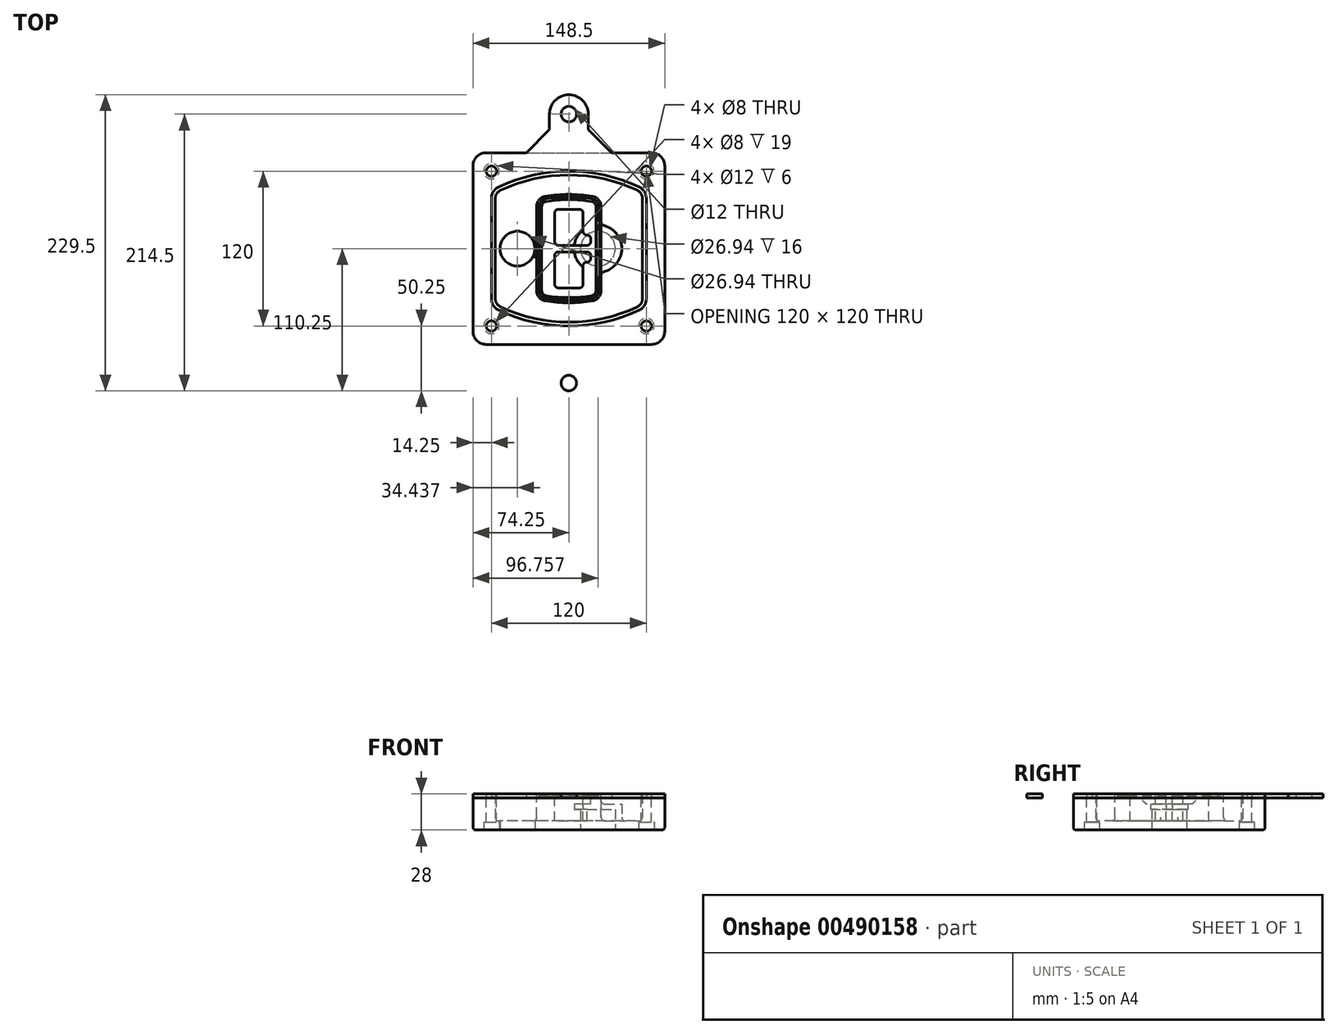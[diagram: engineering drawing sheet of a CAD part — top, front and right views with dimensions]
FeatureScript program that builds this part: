
annotation { "Feature Type Name" : "Feature", "Feature Type Description" : "" }
export const myFeature = defineFeature(function(context is Context, id is Id, definition is map)
    precondition{}
    {
        {
            var Q0;
            Q0=qCreatedBy(makeId("Top.planeOp"),FACE);
            var sketch = newSketch(context, id + "F0", { "sketchPlane" : qUnion([Q0])});
            skPoint(sketch, "E0.rect.middle", {"position": v(0, 0) * mm});
            skLineSegment(sketch, "E1.bottom", {"start": v(-64.25, -74.25) * mm, "end": v(64.25, -74.25) * mm});
            skLineSegment(sketch, "E1.top", {"start": v(-64.25, 74.25) * mm, "end": v(64.25, 74.25) * mm});
            skLineSegment(sketch, "E1.left", {"start": v(-74.25, -64.25) * mm, "end": v(-74.25, 64.25) * mm});
            skLineSegment(sketch, "E1.right", {"start": v(74.25, -64.25) * mm, "end": v(74.25, 64.25) * mm});
            skLineSegment(sketch, "E2", {"start": v(-74.25, 74.25) * mm, "end": v(74.25, -74.25) * mm, "construction": true});
            skLineSegment(sketch, "E3", {"start": v(74.25, 74.25) * mm, "end": v(-74.25, -74.25) * mm, "construction": true});
            skCircle(sketch, "E4", {"center": v(-60, 60) * mm, "radius": 4 * mm});
            skCircle(sketch, "E5", {"center": v(60, 60) * mm, "radius": 4 * mm});
            skCircle(sketch, "E6", {"center": v(60, -60) * mm, "radius": 4 * mm});
            skCircle(sketch, "E7", {"center": v(-60, -60) * mm, "radius": 4 * mm});
            skLineSegment(sketch, "E8", {"start": v(-60, 60) * mm, "end": v(60, 60) * mm, "construction": true});
            skLineSegment(sketch, "E9", {"start": v(60, 60) * mm, "end": v(60, -60) * mm, "construction": true});
            skLineSegment(sketch, "E10", {"start": v(60, -60) * mm, "end": v(-60, -60) * mm, "construction": true});
            skLineSegment(sketch, "E11", {"start": v(-60, -60) * mm, "end": v(-60, 60) * mm, "construction": true});
            skLineSegment(sketch, "E12", {"start": v(-60, 38.83) * mm, "end": v(-60, -38.83) * mm});
            skLineSegment(sketch, "E13", {"start": v(60, 38.83) * mm, "end": v(60, -38.83) * mm});
            skArc(sketch, "E14", {"start": v(54.26, 47.88) * mm, "mid": v(0, 60) * mm, "end": v(-54.26, 47.88) * mm});
            skArc(sketch, "E15", {"start": v(-54.26, -47.88) * mm, "mid": v(0, -60) * mm, "end": v(54.26, -47.88) * mm});
            skLineSegment(sketch, "E16", {"start": v(-60, 0) * mm, "end": v(60, 0) * mm, "construction": true});
            skPoint(sketch, "E17.visualSharp", {"position": v(-60, -45) * mm});
            skArc(sketch, "E17.filletArc", {"start": v(-60, -38.83) * mm, "mid": v(-58.44, -44.2) * mm, "end": v(-54.26, -47.88) * mm});
            skPoint(sketch, "E18.visualSharp", {"position": v(-60, 45) * mm});
            skArc(sketch, "E18.filletArc", {"start": v(-54.26, 47.88) * mm, "mid": v(-58.44, 44.2) * mm, "end": v(-60, 38.83) * mm});
            skPoint(sketch, "E19.visualSharp", {"position": v(60, 45) * mm});
            skArc(sketch, "E19.filletArc", {"start": v(60, 38.83) * mm, "mid": v(58.44, 44.2) * mm, "end": v(54.26, 47.88) * mm});
            skPoint(sketch, "E20.visualSharp", {"position": v(60, -45) * mm});
            skArc(sketch, "E20.filletArc", {"start": v(54.26, -47.88) * mm, "mid": v(58.44, -44.2) * mm, "end": v(60, -38.83) * mm});
            skPoint(sketch, "E21.visualSharp", {"position": v(-74.25, 74.25) * mm});
            skArc(sketch, "E21.filletArc", {"start": v(-64.25, 74.25) * mm, "mid": v(-71.32, 71.32) * mm, "end": v(-74.25, 64.25) * mm});
            skPoint(sketch, "E22.visualSharp", {"position": v(74.25, 74.25) * mm});
            skArc(sketch, "E22.filletArc", {"start": v(74.25, 64.25) * mm, "mid": v(71.32, 71.32) * mm, "end": v(64.25, 74.25) * mm});
            skPoint(sketch, "E23.visualSharp", {"position": v(74.25, -74.25) * mm});
            skArc(sketch, "E23.filletArc", {"start": v(64.25, -74.25) * mm, "mid": v(71.32, -71.32) * mm, "end": v(74.25, -64.25) * mm});
            skPoint(sketch, "E24.visualSharp", {"position": v(-74.25, -74.25) * mm});
            skArc(sketch, "E24.filletArc", {"start": v(-74.25, -64.25) * mm, "mid": v(-71.32, -71.32) * mm, "end": v(-64.25, -74.25) * mm});
            skArc(sketch, "E25.0", {"start": v(57, 38.83) * mm, "mid": v(55.9, 42.58) * mm, "end": v(52.98, 45.17) * mm});
            skLineSegment(sketch, "E25.1", {"start": v(57, 38.83) * mm, "end": v(57, -38.83) * mm});
            skArc(sketch, "E25.2", {"start": v(52.98, -45.17) * mm, "mid": v(55.9, -42.58) * mm, "end": v(57, -38.83) * mm});
            skArc(sketch, "E25.3", {"start": v(-52.98, -45.17) * mm, "mid": v(0, -57) * mm, "end": v(52.98, -45.17) * mm});
            skArc(sketch, "E25.4", {"start": v(-57, -38.83) * mm, "mid": v(-55.9, -42.58) * mm, "end": v(-52.98, -45.17) * mm});
            skArc(sketch, "E25.5", {"start": v(52.98, 45.17) * mm, "mid": v(0, 57) * mm, "end": v(-52.98, 45.17) * mm});
            skLineSegment(sketch, "E25.6", {"start": v(-57, 38.83) * mm, "end": v(-57, -38.83) * mm});
            skArc(sketch, "E25.7", {"start": v(-52.98, 45.17) * mm, "mid": v(-55.9, 42.58) * mm, "end": v(-57, 38.83) * mm});
            skArc(sketch, "E26.0", {"start": v(-55.96, 51.5) * mm, "mid": v(-61.82, 46.33) * mm, "end": v(-64, 38.83) * mm});
            skArc(sketch, "E26.1", {"start": v(55.96, 51.5) * mm, "mid": v(0, 64) * mm, "end": v(-55.96, 51.5) * mm});
            skArc(sketch, "E26.2", {"start": v(64, 38.83) * mm, "mid": v(61.82, 46.33) * mm, "end": v(55.96, 51.5) * mm});
            skLineSegment(sketch, "E26.3", {"start": v(64, 38.83) * mm, "end": v(64, -38.83) * mm});
            skArc(sketch, "E26.4", {"start": v(55.96, -51.5) * mm, "mid": v(61.82, -46.33) * mm, "end": v(64, -38.83) * mm});
            skLineSegment(sketch, "E26.5", {"start": v(-64, 38.83) * mm, "end": v(-64, -38.83) * mm});
            skArc(sketch, "E26.6", {"start": v(-55.96, -51.5) * mm, "mid": v(0, -64) * mm, "end": v(55.96, -51.5) * mm});
            skArc(sketch, "E26.7", {"start": v(-64, -38.83) * mm, "mid": v(-61.82, -46.33) * mm, "end": v(-55.96, -51.5) * mm});
            skSolve(sketch);
        }
        {
            var Q0;
            Q0=makeQuery(id+"F0.imprint","IMPRINT",FACE,{"disambiguationData":[TD([[makeQuery(id+"F0.imprint","IMPRINT",EDGE,{"derivedFrom":sQuery(id+"F0.wireOp",EDGE,"E1.bottom")}),1.0]])]});
            var Q1;
            Q1=makeQuery(id+"F0.imprint","IMPRINT",FACE,{"disambiguationData":[TD([[makeQuery(id+"F0.imprint","IMPRINT",EDGE,{"derivedFrom":sQuery(id+"F0.wireOp",EDGE,"E12")}),1.0]])]});
            var Q2;
            Q2=makeQuery(id+"F0.imprint","IMPRINT",FACE,{"disambiguationData":[TD([[makeQuery(id+"F0.imprint","IMPRINT",EDGE,{"derivedFrom":sQuery(id+"F0.wireOp",EDGE,"E25.0")}),1.0]])]});
            var Q3;
            Q3=makeQuery(id+"F0.imprint","IMPRINT",FACE,{"disambiguationData":[TD([[makeQuery(id+"F0.imprint","IMPRINT",EDGE,{"derivedFrom":sQuery(id+"F0.wireOp",EDGE,"E12")}),-1.0]])]});
            extrude(context, id + "F1", {"entities" : qUnion([Q0, Q1, Q2, Q3]), "oppositeDirection" : true, "depth" : 25 * mm});
        }
        {
            var Q0;
            Q0=makeQuery(id+"F0.imprint","IMPRINT",FACE,{"disambiguationData":[TD([[makeQuery(id+"F0.imprint","IMPRINT",EDGE,{"derivedFrom":sQuery(id+"F0.wireOp",EDGE,"E12")}),1.0]])]});
            extrude(context, id + "F2", {"entities" : qUnion([Q0]), "operationType" : NewBodyOperationType.ADD, "depth" : 3 * mm});
        }
        {
            var Q0;
            Q0=makeQuery(id+"F0.imprint","IMPRINT",FACE,{"disambiguationData":[TD([[makeQuery(id+"F0.imprint","IMPRINT",EDGE,{"derivedFrom":sQuery(id+"F0.wireOp",EDGE,"E25.0")}),1.0]])]});
            extrude(context, id + "F3", {"entities" : qUnion([Q0]), "operationType" : NewBodyOperationType.REMOVE, "oppositeDirection" : true, "depth" : 18 * mm});
        }
        {
            var Q0;
            Q0=makeQuery(id+"F2.opExtrude","CAP_FACE",FACE,{"disambiguationData":[OSD([sQuery(id+"F0.wireOp",EDGE,"E12"),sQuery(id+"F0.wireOp",EDGE,"E13"),sQuery(id+"F0.wireOp",EDGE,"E14"),sQuery(id+"F0.wireOp",EDGE,"E15"),sQuery(id+"F0.wireOp",EDGE,"E17.filletArc"),sQuery(id+"F0.wireOp",EDGE,"E18.filletArc"),sQuery(id+"F0.wireOp",EDGE,"E19.filletArc"),sQuery(id+"F0.wireOp",EDGE,"E20.filletArc"),sQuery(id+"F0.wireOp",EDGE,"E25.0"),sQuery(id+"F0.wireOp",EDGE,"E25.1"),sQuery(id+"F0.wireOp",EDGE,"E25.2"),sQuery(id+"F0.wireOp",EDGE,"E25.3"),sQuery(id+"F0.wireOp",EDGE,"E25.4"),sQuery(id+"F0.wireOp",EDGE,"E25.5"),sQuery(id+"F0.wireOp",EDGE,"E25.6"),sQuery(id+"F0.wireOp",EDGE,"E25.7")])],"isStart":false});
            var sketch = newSketch(context, id + "F4", { "sketchPlane" : qUnion([Q0])});
            skArc(sketch, "E27.0", {"start": v(-18.34, -40.45) * mm, "mid": v(0, -42) * mm, "end": v(18.34, -40.45) * mm});
            skArc(sketch, "E28.0", {"start": v(18.34, 40.45) * mm, "mid": v(0, 42) * mm, "end": v(-18.34, 40.45) * mm});
            skLineSegment(sketch, "E29", {"start": v(-25, 32.57) * mm, "end": v(-25, -32.57) * mm});
            skLineSegment(sketch, "E30", {"start": v(25, 32.57) * mm, "end": v(25, -32.57) * mm});
            skLineSegment(sketch, "E31", {"start": v(-25, 39.1) * mm, "end": v(25, 39.1) * mm, "construction": true});
            skLineSegment(sketch, "E32", {"start": v(-25, -39.1) * mm, "end": v(25, -39.1) * mm, "construction": true});
            skPoint(sketch, "E33.visualSharp", {"position": v(-25, 39.1) * mm});
            skArc(sketch, "E33.filletArc", {"start": v(-18.34, 40.45) * mm, "mid": v(-23.11, 37.73) * mm, "end": v(-25, 32.57) * mm});
            skPoint(sketch, "E34.visualSharp", {"position": v(25, 39.1) * mm});
            skArc(sketch, "E34.filletArc", {"start": v(25, 32.57) * mm, "mid": v(23.11, 37.73) * mm, "end": v(18.34, 40.45) * mm});
            skPoint(sketch, "E35.visualSharp", {"position": v(25, -39.1) * mm});
            skArc(sketch, "E35.filletArc", {"start": v(18.34, -40.45) * mm, "mid": v(23.11, -37.73) * mm, "end": v(25, -32.57) * mm});
            skPoint(sketch, "E36.visualSharp", {"position": v(-25, -39.1) * mm});
            skArc(sketch, "E36.filletArc", {"start": v(-25, -32.57) * mm, "mid": v(-23.11, -37.73) * mm, "end": v(-18.34, -40.45) * mm});
            skArc(sketch, "E37.0", {"start": v(52.98, 45.17) * mm, "mid": v(0, 57) * mm, "end": v(-52.98, 45.17) * mm});
            skArc(sketch, "E37.1", {"start": v(-52.98, 45.17) * mm, "mid": v(-55.9, 42.58) * mm, "end": v(-57, 38.83) * mm});
            skLineSegment(sketch, "E37.2", {"start": v(-57, 38.83) * mm, "end": v(-57, -38.83) * mm});
            skArc(sketch, "E37.3", {"start": v(-57, -38.83) * mm, "mid": v(-55.9, -42.58) * mm, "end": v(-52.98, -45.17) * mm});
            skArc(sketch, "E37.4", {"start": v(-52.98, -45.17) * mm, "mid": v(0, -57) * mm, "end": v(52.98, -45.17) * mm});
            skArc(sketch, "E37.5", {"start": v(52.98, -45.17) * mm, "mid": v(55.9, -42.58) * mm, "end": v(57, -38.83) * mm});
            skLineSegment(sketch, "E37.6", {"start": v(57, 38.83) * mm, "end": v(57, -38.83) * mm});
            skArc(sketch, "E37.7", {"start": v(57, 38.83) * mm, "mid": v(55.9, 42.58) * mm, "end": v(52.98, 45.17) * mm});
            skLineSegment(sketch, "E38.0", {"start": v(23, 32.57) * mm, "end": v(23, -32.57) * mm});
            skArc(sketch, "E38.1", {"start": v(18, -38.48) * mm, "mid": v(21.58, -36.44) * mm, "end": v(23, -32.57) * mm});
            skArc(sketch, "E38.2", {"start": v(-18, -38.48) * mm, "mid": v(0, -40) * mm, "end": v(18, -38.48) * mm});
            skArc(sketch, "E38.3", {"start": v(-23, -32.57) * mm, "mid": v(-21.58, -36.44) * mm, "end": v(-18, -38.48) * mm});
            skLineSegment(sketch, "E38.4", {"start": v(-23, 32.57) * mm, "end": v(-23, -32.57) * mm});
            skArc(sketch, "E38.5", {"start": v(23, 32.57) * mm, "mid": v(21.58, 36.44) * mm, "end": v(18, 38.48) * mm});
            skArc(sketch, "E38.6", {"start": v(-18, 38.48) * mm, "mid": v(-21.58, 36.44) * mm, "end": v(-23, 32.57) * mm});
            skArc(sketch, "E38.7", {"start": v(18, 38.48) * mm, "mid": v(0, 40) * mm, "end": v(-18, 38.48) * mm});
            skArc(sketch, "E39.0", {"start": v(21, 32.57) * mm, "mid": v(20.06, 35.15) * mm, "end": v(17.67, 36.5) * mm});
            skLineSegment(sketch, "E39.1", {"start": v(21, 32.57) * mm, "end": v(21, -32.57) * mm});
            skArc(sketch, "E39.2", {"start": v(17.67, -36.5) * mm, "mid": v(20.06, -35.15) * mm, "end": v(21, -32.57) * mm});
            skArc(sketch, "E39.3", {"start": v(-17.67, -36.5) * mm, "mid": v(0, -38) * mm, "end": v(17.67, -36.5) * mm});
            skArc(sketch, "E39.4", {"start": v(-21, -32.57) * mm, "mid": v(-20.06, -35.15) * mm, "end": v(-17.67, -36.5) * mm});
            skArc(sketch, "E39.5", {"start": v(17.67, 36.5) * mm, "mid": v(0, 38) * mm, "end": v(-17.67, 36.5) * mm});
            skLineSegment(sketch, "E39.6", {"start": v(-21, 32.57) * mm, "end": v(-21, -32.57) * mm});
            skArc(sketch, "E39.7", {"start": v(-17.67, 36.5) * mm, "mid": v(-20.06, 35.15) * mm, "end": v(-21, 32.57) * mm});
            skLineSegment(sketch, "E40", {"start": v(-25, 0) * mm, "end": v(25, 0) * mm, "construction": true});
            skLineSegment(sketch, "E41", {"start": v(-11, 5.5) * mm, "end": v(-11, 27.5) * mm});
            skLineSegment(sketch, "E42", {"start": v(-8, 30.5) * mm, "end": v(8, 30.5) * mm});
            skLineSegment(sketch, "E43", {"start": v(11, 27.5) * mm, "end": v(11, 13.5) * mm});
            skLineSegment(sketch, "E44", {"start": v(14, 10.5) * mm, "end": v(14, 10.5) * mm});
            skLineSegment(sketch, "E45", {"start": v(17, 7.5) * mm, "end": v(17, 5.5) * mm});
            skLineSegment(sketch, "E46", {"start": v(14, 2.5) * mm, "end": v(-8, 2.5) * mm});
            skPoint(sketch, "E47.visualSharp", {"position": v(-11, 30.5) * mm});
            skArc(sketch, "E47.filletArc", {"start": v(-8, 30.5) * mm, "mid": v(-10.12, 29.62) * mm, "end": v(-11, 27.5) * mm});
            skPoint(sketch, "E48.visualSharp", {"position": v(11, 30.5) * mm});
            skArc(sketch, "E48.filletArc", {"start": v(11, 27.5) * mm, "mid": v(10.12, 29.62) * mm, "end": v(8, 30.5) * mm});
            skPoint(sketch, "E49.visualSharp", {"position": v(11, 10.5) * mm});
            skArc(sketch, "E49.filletArc", {"start": v(11, 13.5) * mm, "mid": v(11.88, 11.38) * mm, "end": v(14, 10.5) * mm});
            skPoint(sketch, "E50.visualSharp", {"position": v(17, 10.5) * mm});
            skArc(sketch, "E50.filletArc", {"start": v(17, 7.5) * mm, "mid": v(16.12, 9.62) * mm, "end": v(14, 10.5) * mm});
            skPoint(sketch, "E51.visualSharp", {"position": v(17, 2.5) * mm});
            skArc(sketch, "E51.filletArc", {"start": v(14, 2.5) * mm, "mid": v(16.12, 3.38) * mm, "end": v(17, 5.5) * mm});
            skPoint(sketch, "E52.visualSharp", {"position": v(-11, 2.5) * mm});
            skArc(sketch, "E52.filletArc", {"start": v(-11, 5.5) * mm, "mid": v(-10.12, 3.38) * mm, "end": v(-8, 2.5) * mm});
            skLineSegment(sketch, "E53.0.MirrorCS", {"start": v(14, -2.5) * mm, "end": v(-8, -2.5) * mm});
            skArc(sketch, "E54.0.MirrorCS", {"start": v(-11, -5.5) * mm, "mid": v(-10.12, -3.38) * mm, "end": v(-8, -2.5) * mm});
            skLineSegment(sketch, "E55.0.MirrorCS", {"start": v(-11, -5.5) * mm, "end": v(-11, -27.5) * mm});
            skArc(sketch, "E56.0.MirrorCS", {"start": v(-8, -30.5) * mm, "mid": v(-10.12, -29.62) * mm, "end": v(-11, -27.5) * mm});
            skLineSegment(sketch, "E57.0.MirrorCS", {"start": v(-8, -30.5) * mm, "end": v(8, -30.5) * mm});
            skArc(sketch, "E58.0.MirrorCS", {"start": v(11, -27.5) * mm, "mid": v(10.12, -29.62) * mm, "end": v(8, -30.5) * mm});
            skLineSegment(sketch, "E59.0.MirrorCS", {"start": v(11, -27.5) * mm, "end": v(11, -13.5) * mm});
            skArc(sketch, "E60.0.MirrorCS", {"start": v(11, -13.5) * mm, "mid": v(11.88, -11.38) * mm, "end": v(14, -10.5) * mm});
            skArc(sketch, "E61.0.MirrorCS", {"start": v(17, -7.5) * mm, "mid": v(16.12, -9.62) * mm, "end": v(14, -10.5) * mm});
            skLineSegment(sketch, "E62.0.MirrorCS", {"start": v(17, -7.5) * mm, "end": v(17, -5.5) * mm});
            skArc(sketch, "E63.0.MirrorCS", {"start": v(14, -2.5) * mm, "mid": v(16.12, -3.38) * mm, "end": v(17, -5.5) * mm});
            skSolve(sketch);
        }
        {
            var Q0;
            Q0=makeQuery(id+"F4.imprint","IMPRINT",FACE,{"disambiguationData":[TD([[makeQuery(id+"F4.imprint","IMPRINT",EDGE,{"derivedFrom":sQuery(id+"F4.wireOp",EDGE,"E27.0")}),1.0]])]});
            var Q1;
            Q1=makeQuery(id+"F4.imprint","IMPRINT",FACE,{"disambiguationData":[TD([[makeQuery(id+"F4.imprint","IMPRINT",EDGE,{"derivedFrom":sQuery(id+"F4.wireOp",EDGE,"E38.0")}),-1.0]])]});
            var Q2;
            Q2=makeQuery(id+"F4.imprint","IMPRINT",FACE,{"disambiguationData":[TD([[makeQuery(id+"F4.imprint","IMPRINT",EDGE,{"derivedFrom":sQuery(id+"F4.wireOp",EDGE,"E39.0")}),1.0]])]});
            extrude(context, id + "F5", {"entities" : qUnion([Q0, Q1, Q2]), "operationType" : NewBodyOperationType.ADD, "endBound" : BoundingType.UP_TO_NEXT, "oppositeDirection" : true, "depth" : 25 * mm});
        }
        {
            var Q0;
            Q0=makeQuery(id+"F4.imprint","IMPRINT",FACE,{"disambiguationData":[TD([[makeQuery(id+"F4.imprint","IMPRINT",EDGE,{"derivedFrom":sQuery(id+"F4.wireOp",EDGE,"E38.0")}),-1.0]])]});
            extrude(context, id + "F6", {"entities" : qUnion([Q0]), "operationType" : NewBodyOperationType.REMOVE, "oppositeDirection" : true, "depth" : 2 * mm});
        }
        {
            var Q0;
            Q0=makeQuery(id+"F1.opExtrude","CAP_FACE",FACE,{"disambiguationData":[OSD([sQuery(id+"F0.wireOp",EDGE,"E1.bottom"),sQuery(id+"F0.wireOp",EDGE,"E1.top"),sQuery(id+"F0.wireOp",EDGE,"E1.left"),sQuery(id+"F0.wireOp",EDGE,"E1.right"),sQuery(id+"F0.wireOp",EDGE,"E4"),sQuery(id+"F0.wireOp",EDGE,"E5"),sQuery(id+"F0.wireOp",EDGE,"E6"),sQuery(id+"F0.wireOp",EDGE,"E7"),sQuery(id+"F0.wireOp",EDGE,"E21.filletArc"),sQuery(id+"F0.wireOp",EDGE,"E22.filletArc"),sQuery(id+"F0.wireOp",EDGE,"E23.filletArc"),sQuery(id+"F0.wireOp",EDGE,"E24.filletArc")])],"isStart":false});
            var sketch = newSketch(context, id + "F7", { "sketchPlane" : qUnion([Q0])});
            skCircle(sketch, "E64", {"center": v(22.5, 0) * mm, "radius": 13.47 * mm});
            skCircle(sketch, "E65", {"center": v(-39.81, 0) * mm, "radius": 13.47 * mm});
            skLineSegment(sketch, "E66", {"start": v(74.25, 0) * mm, "end": v(-74.25, 0) * mm});
            skCircle(sketch, "E67", {"center": v(22.5, 0) * mm, "radius": 18.47 * mm});
            skCircle(sketch, "E68", {"center": v(60, -60) * mm, "radius": 6 * mm});
            skCircle(sketch, "E69", {"center": v(-60, -60) * mm, "radius": 6 * mm});
            skCircle(sketch, "E70", {"center": v(-60, 60) * mm, "radius": 6 * mm});
            skCircle(sketch, "E71", {"center": v(60, 60) * mm, "radius": 6 * mm});
            skSolve(sketch);
        }
        {
            var Q0;
            {var subQ1=sQuery(id+"F7.wireOp",EDGE,"E66");var subQ4=sQuery(id+"F7.wireOp",EDGE,"E64");var subQ6=makeQuery(id+"F7.imprint","INTERSECT",VERTEX,{"disambiguationData":[OD(0.0)],"derivedFrom":[subQ4,subQ1]});Q0=makeQuery(id+"F7.imprint","IMPRINT",FACE,{"disambiguationData":[TD([[makeQuery(id+"F7.imprint","IMPRINT",EDGE,{"disambiguationData":[TD([[subQ6,-1.0]])],"derivedFrom":subQ4}),-1.0]])]});}
            var Q1;
            {var subQ0=sQuery(id+"F7.wireOp",EDGE,"E66");var subQ1=sQuery(id+"F7.wireOp",EDGE,"E64");var subQ3=makeQuery(id+"F7.imprint","INTERSECT",VERTEX,{"disambiguationData":[OD(0.0)],"derivedFrom":[subQ1,subQ0]});Q1=makeQuery(id+"F7.imprint","IMPRINT",FACE,{"disambiguationData":[TD([[makeQuery(id+"F7.imprint","IMPRINT",EDGE,{"disambiguationData":[TD([[subQ3,-1.0]])],"derivedFrom":subQ1}),1.0]])]});}
            var Q2;
            {var subQ0=sQuery(id+"F7.wireOp",EDGE,"E66");var subQ1=sQuery(id+"F7.wireOp",EDGE,"E64");var subQ3=makeQuery(id+"F7.imprint","INTERSECT",VERTEX,{"disambiguationData":[OD(0.0)],"derivedFrom":[subQ1,subQ0]});Q2=makeQuery(id+"F7.imprint","IMPRINT",FACE,{"disambiguationData":[TD([[makeQuery(id+"F7.imprint","IMPRINT",EDGE,{"disambiguationData":[TD([[subQ3,1.0]])],"derivedFrom":subQ1}),1.0]])]});}
            var Q3;
            {var subQ1=sQuery(id+"F7.wireOp",EDGE,"E66");var subQ4=sQuery(id+"F7.wireOp",EDGE,"E64");var subQ6=makeQuery(id+"F7.imprint","INTERSECT",VERTEX,{"disambiguationData":[OD(0.0)],"derivedFrom":[subQ4,subQ1]});Q3=makeQuery(id+"F7.imprint","IMPRINT",FACE,{"disambiguationData":[TD([[makeQuery(id+"F7.imprint","IMPRINT",EDGE,{"disambiguationData":[TD([[subQ6,1.0]])],"derivedFrom":subQ4}),-1.0]])]});}
            extrude(context, id + "F8", {"entities" : qUnion([Q0, Q1, Q2, Q3]), "operationType" : NewBodyOperationType.ADD, "oppositeDirection" : true, "depth" : 20 * mm});
        }
        {
            var Q0;
            {var subQ0=sQuery(id+"F7.wireOp",EDGE,"E66");var subQ1=sQuery(id+"F7.wireOp",EDGE,"E64");var subQ3=makeQuery(id+"F7.imprint","INTERSECT",VERTEX,{"disambiguationData":[OD(0.0)],"derivedFrom":[subQ1,subQ0]});Q0=makeQuery(id+"F7.imprint","IMPRINT",FACE,{"disambiguationData":[TD([[makeQuery(id+"F7.imprint","IMPRINT",EDGE,{"disambiguationData":[TD([[subQ3,-1.0]])],"derivedFrom":subQ1}),1.0]])]});}
            var Q1;
            {var subQ0=sQuery(id+"F7.wireOp",EDGE,"E66");var subQ1=sQuery(id+"F7.wireOp",EDGE,"E64");var subQ3=makeQuery(id+"F7.imprint","INTERSECT",VERTEX,{"disambiguationData":[OD(0.0)],"derivedFrom":[subQ1,subQ0]});Q1=makeQuery(id+"F7.imprint","IMPRINT",FACE,{"disambiguationData":[TD([[makeQuery(id+"F7.imprint","IMPRINT",EDGE,{"disambiguationData":[TD([[subQ3,1.0]])],"derivedFrom":subQ1}),1.0]])]});}
            extrude(context, id + "F9", {"entities" : qUnion([Q0, Q1]), "operationType" : NewBodyOperationType.REMOVE, "oppositeDirection" : true, "depth" : 16 * mm});
        }
        {
            var Q0;
            {var subQ0=sQuery(id+"F7.wireOp",EDGE,"E66");var subQ1=sQuery(id+"F7.wireOp",EDGE,"E65");var subQ3=makeQuery(id+"F7.imprint","INTERSECT",VERTEX,{"disambiguationData":[OD(0.0)],"derivedFrom":[subQ1,subQ0]});Q0=makeQuery(id+"F7.imprint","IMPRINT",FACE,{"disambiguationData":[TD([[makeQuery(id+"F7.imprint","IMPRINT",EDGE,{"disambiguationData":[TD([[subQ3,-1.0]])],"derivedFrom":subQ1}),1.0]])]});}
            var Q1;
            {var subQ0=sQuery(id+"F7.wireOp",EDGE,"E66");var subQ1=sQuery(id+"F7.wireOp",EDGE,"E65");var subQ3=makeQuery(id+"F7.imprint","INTERSECT",VERTEX,{"disambiguationData":[OD(0.0)],"derivedFrom":[subQ1,subQ0]});Q1=makeQuery(id+"F7.imprint","IMPRINT",FACE,{"disambiguationData":[TD([[makeQuery(id+"F7.imprint","IMPRINT",EDGE,{"disambiguationData":[TD([[subQ3,1.0]])],"derivedFrom":subQ1}),1.0]])]});}
            extrude(context, id + "F10", {"entities" : qUnion([Q0, Q1]), "operationType" : NewBodyOperationType.REMOVE, "oppositeDirection" : true, "depth" : 25 * mm});
        }
        {
            var Q0;
            Q0=makeQuery(id+"F7.imprint","IMPRINT",FACE,{"disambiguationData":[TD([[makeQuery(id+"F7.imprint","IMPRINT",EDGE,{"derivedFrom":sQuery(id+"F7.wireOp",EDGE,"E68")}),1.0]])]});
            var Q1;
            Q1=makeQuery(id+"F7.imprint","IMPRINT",FACE,{"disambiguationData":[TD([[makeQuery(id+"F7.imprint","IMPRINT",EDGE,{"derivedFrom":makeQuery(id+"F1.opExtrude","CAP_EDGE",EDGE,{"disambiguationData":[OSD([sQuery(id+"F0.wireOp",EDGE,"E5")])],"isStart":false})}),-1.0]])]});
            var Q2;
            Q2=makeQuery(id+"F7.imprint","IMPRINT",FACE,{"disambiguationData":[TD([[makeQuery(id+"F7.imprint","IMPRINT",EDGE,{"derivedFrom":sQuery(id+"F7.wireOp",EDGE,"E69")}),1.0]])]});
            var Q3;
            Q3=makeQuery(id+"F7.imprint","IMPRINT",FACE,{"disambiguationData":[TD([[makeQuery(id+"F7.imprint","IMPRINT",EDGE,{"derivedFrom":makeQuery(id+"F1.opExtrude","CAP_EDGE",EDGE,{"disambiguationData":[OSD([sQuery(id+"F0.wireOp",EDGE,"E4")])],"isStart":false})}),-1.0]])]});
            var Q4;
            Q4=makeQuery(id+"F7.imprint","IMPRINT",FACE,{"disambiguationData":[TD([[makeQuery(id+"F7.imprint","IMPRINT",EDGE,{"derivedFrom":sQuery(id+"F7.wireOp",EDGE,"E70")}),1.0]])]});
            var Q5;
            Q5=makeQuery(id+"F7.imprint","IMPRINT",FACE,{"disambiguationData":[TD([[makeQuery(id+"F7.imprint","IMPRINT",EDGE,{"derivedFrom":makeQuery(id+"F1.opExtrude","CAP_EDGE",EDGE,{"disambiguationData":[OSD([sQuery(id+"F0.wireOp",EDGE,"E7")])],"isStart":false})}),-1.0]])]});
            var Q6;
            Q6=makeQuery(id+"F7.imprint","IMPRINT",FACE,{"disambiguationData":[TD([[makeQuery(id+"F7.imprint","IMPRINT",EDGE,{"derivedFrom":sQuery(id+"F7.wireOp",EDGE,"E71")}),1.0]])]});
            var Q7;
            Q7=makeQuery(id+"F7.imprint","IMPRINT",FACE,{"disambiguationData":[TD([[makeQuery(id+"F7.imprint","IMPRINT",EDGE,{"derivedFrom":makeQuery(id+"F1.opExtrude","CAP_EDGE",EDGE,{"disambiguationData":[OSD([sQuery(id+"F0.wireOp",EDGE,"E6")])],"isStart":false})}),-1.0]])]});
            extrude(context, id + "F11", {"entities" : qUnion([Q0, Q1, Q2, Q3, Q4, Q5, Q6, Q7]), "operationType" : NewBodyOperationType.REMOVE, "oppositeDirection" : true, "depth" : 6 * mm});
        }
        {
            var Q0;
            Q0=makeQuery(id+"F9.boolean.opBoolean","COPY",FACE,{"derivedFrom":makeQuery(id+"F9.opExtrude","CAP_FACE",FACE,{"disambiguationData":[OSD([sQuery(id+"F7.wireOp",EDGE,"E64")])],"isStart":false})});
            var sketch = newSketch(context, id + "F12", { "sketchPlane" : qUnion([Q0])});
            skArc(sketch, "E72.0", {"start": v(11, 14.45) * mm, "mid": v(6.45, 9.13) * mm, "end": v(4.2, 2.5) * mm});
            skArc(sketch, "E72.1", {"start": v(4.2, -2.5) * mm, "mid": v(6.45, -9.13) * mm, "end": v(11, -14.45) * mm});
            skLineSegment(sketch, "E73", {"start": v(4.2, -2.5) * mm, "end": v(14, -2.5) * mm});
            skLineSegment(sketch, "E74.0", {"start": v(14, 2.5) * mm, "end": v(4.2, 2.5) * mm});
            skArc(sketch, "E74.1", {"start": v(14, 2.5) * mm, "mid": v(16.12, 3.38) * mm, "end": v(17, 5.5) * mm});
            skLineSegment(sketch, "E74.2", {"start": v(17, 7.5) * mm, "end": v(17, 5.5) * mm});
            skArc(sketch, "E74.3", {"start": v(17, 7.5) * mm, "mid": v(16.12, 9.62) * mm, "end": v(14, 10.5) * mm});
            skArc(sketch, "E74.4", {"start": v(11, 13.5) * mm, "mid": v(11.88, 11.38) * mm, "end": v(14, 10.5) * mm});
            skLineSegment(sketch, "E74.5", {"start": v(11, 14.45) * mm, "end": v(11, 13.5) * mm});
            skLineSegment(sketch, "E74.7", {"start": v(14, -2.5) * mm, "end": v(4.2, -2.5) * mm});
            skArc(sketch, "E74.8", {"start": v(14, -2.5) * mm, "mid": v(16.12, -3.38) * mm, "end": v(17, -5.5) * mm});
            skLineSegment(sketch, "E74.9", {"start": v(17, -7.5) * mm, "end": v(17, -5.5) * mm});
            skArc(sketch, "E74.10", {"start": v(17, -7.5) * mm, "mid": v(16.12, -9.62) * mm, "end": v(14, -10.5) * mm});
            skArc(sketch, "E74.11", {"start": v(11, -13.5) * mm, "mid": v(11.88, -11.38) * mm, "end": v(14, -10.5) * mm});
            skLineSegment(sketch, "E74.12", {"start": v(11, -14.45) * mm, "end": v(11, -13.5) * mm});
            skPoint(sketch, "E75.orphan", {"position": v(11, -27.5) * mm});
            skPoint(sketch, "E76.orphan", {"position": v(-8, -2.5) * mm});
            skPoint(sketch, "E77.orphan", {"position": v(-8, 2.5) * mm});
            skPoint(sketch, "E78.orphan", {"position": v(11, 27.5) * mm});
            skSolve(sketch);
        }
        {
            var Q0;
            {var subQ7=sQuery(id+"F12.wireOp",EDGE,"E72.0");var subQ14=sQuery(id+"F12.wireOp",EDGE,"E72.1");var subQ16=sQuery(id+"F12.wireOp",EDGE,"E74.1");var subQ18=sQuery(id+"F12.wireOp",EDGE,"E74.8");Q0=qUnion([makeQuery(id+"F12.imprint","IMPRINT",FACE,{"disambiguationData":[TD([[makeQuery(id+"F12.imprint","IMPRINT",EDGE,{"derivedFrom":subQ7}),1.0]])]}),makeQuery(id+"F12.imprint","IMPRINT",FACE,{"disambiguationData":[TD([[makeQuery(id+"F12.imprint","IMPRINT",EDGE,{"derivedFrom":subQ14}),1.0]])]}),makeQuery(id+"F12.imprint","IMPRINT",FACE,{"disambiguationData":[TD([[makeQuery(id+"F12.imprint","IMPRINT",EDGE,{"derivedFrom":subQ16}),1.0]])]}),makeQuery(id+"F12.imprint","IMPRINT",FACE,{"disambiguationData":[TD([[makeQuery(id+"F12.imprint","IMPRINT",EDGE,{"derivedFrom":subQ18}),-1.0]])]})]);}
            var Q1;
            Q1=makeQuery(id+"F5.boolean.opBoolean","SPLIT",FACE,{"disambiguationData":[TD([makeQuery(id+"F5.opExtrude","SWEPT_FACE",FACE,{"disambiguationData":[OSD([sQuery(id+"F4.wireOp",EDGE,"E41")])]})])],"derivedFrom":makeQuery(id+"F3.boolean.opBoolean","COPY",FACE,{"derivedFrom":makeQuery(id+"F3.opExtrude","CAP_FACE",FACE,{"disambiguationData":[OSD([sQuery(id+"F0.wireOp",EDGE,"E25.0"),sQuery(id+"F0.wireOp",EDGE,"E25.1"),sQuery(id+"F0.wireOp",EDGE,"E25.2"),sQuery(id+"F0.wireOp",EDGE,"E25.3"),sQuery(id+"F0.wireOp",EDGE,"E25.4"),sQuery(id+"F0.wireOp",EDGE,"E25.5"),sQuery(id+"F0.wireOp",EDGE,"E25.6"),sQuery(id+"F0.wireOp",EDGE,"E25.7")])],"isStart":false})})});
            extrude(context, id + "F13", {"entities" : qUnion([Q0]), "operationType" : NewBodyOperationType.REMOVE, "endBound" : BoundingType.UP_TO_SURFACE, "endBoundEntityFace" : qUnion([Q1]), "depth" : 25 * mm});
        }
        {
            var Q0;
            Q0=makeQuery(id+"F3.boolean.opBoolean","COPY",EDGE,{"derivedFrom":makeQuery(id+"F3.opExtrude","CAP_EDGE",EDGE,{"disambiguationData":[OSD([sQuery(id+"F0.wireOp",EDGE,"E25.6")])],"isStart":false})});
            var Q1;
            Q1=makeQuery(id+"F8.boolean.opBoolean","INTERSECT",EDGE,{"derivedFrom":[makeQuery(id+"F5.opExtrude","SWEPT_FACE",FACE,{"disambiguationData":[OSD([sQuery(id+"F4.wireOp",EDGE,"E30")])]}),makeQuery(id+"F8.opExtrude","CAP_FACE",FACE,{"disambiguationData":[OSD([sQuery(id+"F7.wireOp",EDGE,"E67")])],"isStart":false})]});
            var Q2;
            Q2=makeQuery(id+"F8.boolean.opBoolean","INTERSECT",EDGE,{"disambiguationData":[OD(1.0)],"derivedFrom":[makeQuery(id+"F5.opExtrude","SWEPT_FACE",FACE,{"disambiguationData":[OSD([sQuery(id+"F4.wireOp",EDGE,"E30")])]}),makeQuery(id+"F8.opExtrude","SWEPT_FACE",FACE,{"disambiguationData":[OSD([sQuery(id+"F7.wireOp",EDGE,"E67")])]})]});
            var Q3;
            {var subQ0=sQuery(id+"F4.wireOp",EDGE,"E30");Q3=makeQuery(id+"F8.boolean.opBoolean","SPLIT",EDGE,{"disambiguationData":[TD([makeQuery(id+"F5.opExtrude","SWEPT_FACE",FACE,{"disambiguationData":[OSD([sQuery(id+"F4.wireOp",EDGE,"E35.filletArc")])]})])],"derivedFrom":makeQuery(id+"F5.opExtrude","CAP_EDGE",EDGE,{"disambiguationData":[OSD([subQ0])],"isStart":false})});}
            var Q4;
            {var subQ0=sQuery(id+"F0.wireOp",EDGE,"E25.7");var subQ1=sQuery(id+"F0.wireOp",EDGE,"E25.1");var subQ2=sQuery(id+"F0.wireOp",EDGE,"E25.6");var subQ3=sQuery(id+"F0.wireOp",EDGE,"E25.5");var subQ4=sQuery(id+"F0.wireOp",EDGE,"E25.4");var subQ5=sQuery(id+"F0.wireOp",EDGE,"E25.0");var subQ6=sQuery(id+"F0.wireOp",EDGE,"E25.2");var subQ7=sQuery(id+"F0.wireOp",EDGE,"E25.3");Q4=makeQuery(id+"F8.boolean.opBoolean","INTERSECT",EDGE,{"derivedFrom":[makeQuery(id+"F5.boolean.opBoolean","SPLIT",FACE,{"disambiguationData":[TD([makeQuery(id+"F2.opExtrude","SWEPT_FACE",FACE,{"disambiguationData":[OSD([subQ5])]})])],"derivedFrom":makeQuery(id+"F3.boolean.opBoolean","COPY",FACE,{"derivedFrom":makeQuery(id+"F3.opExtrude","CAP_FACE",FACE,{"disambiguationData":[OSD([subQ5,subQ1,subQ6,subQ7,subQ4,subQ3,subQ2,subQ0])],"isStart":false})})}),makeQuery(id+"F8.opExtrude","SWEPT_FACE",FACE,{"disambiguationData":[OSD([sQuery(id+"F7.wireOp",EDGE,"E67")])]})]});}
            var Q5;
            Q5=makeQuery(id+"F8.boolean.opBoolean","INTERSECT",EDGE,{"disambiguationData":[OD(0.0)],"derivedFrom":[makeQuery(id+"F5.opExtrude","SWEPT_FACE",FACE,{"disambiguationData":[OSD([sQuery(id+"F4.wireOp",EDGE,"E30")])]}),makeQuery(id+"F8.opExtrude","SWEPT_FACE",FACE,{"disambiguationData":[OSD([sQuery(id+"F7.wireOp",EDGE,"E67")])]})]});
            fillet(context, id + "F14", {"entities" : qUnion([Q0, Q1, Q2, Q3, Q4, Q5]), "radius" : 3 * mm, "tangentPropagation" : true, "allowEdgeOverflow" : false});
        }
        {
            var Q0;
            Q0=makeQuery(id+"F1.opExtrude","CAP_EDGE",EDGE,{"disambiguationData":[OSD([sQuery(id+"F0.wireOp",EDGE,"E1.bottom")])],"isStart":false});
            fillet(context, id + "F15", {"entities" : qUnion([Q0]), "radius" : 2 * mm, "tangentPropagation" : true, "allowEdgeOverflow" : false});
        }
        {
            var Q0;
            {var subQ0=sQuery(id+"F0.wireOp",EDGE,"E21.filletArc");var subQ1=sQuery(id+"F0.wireOp",EDGE,"E7");var subQ2=sQuery(id+"F0.wireOp",EDGE,"E6");var subQ3=sQuery(id+"F0.wireOp",EDGE,"E5");var subQ4=sQuery(id+"F0.wireOp",EDGE,"E4");var subQ5=sQuery(id+"F0.wireOp",EDGE,"E22.filletArc");var subQ6=sQuery(id+"F0.wireOp",EDGE,"E1.bottom");var subQ7=sQuery(id+"F0.wireOp",EDGE,"E1.right");var subQ8=sQuery(id+"F0.wireOp",EDGE,"E1.top");var subQ9=sQuery(id+"F0.wireOp",EDGE,"E1.left");var subQ10=sQuery(id+"F0.wireOp",EDGE,"E23.filletArc");var subQ11=sQuery(id+"F0.wireOp",EDGE,"E24.filletArc");Q0=makeQuery(id+"F2.boolean.opBoolean","SPLIT",FACE,{"disambiguationData":[TD([makeQuery(id+"F1.opExtrude","SWEPT_FACE",FACE,{"disambiguationData":[OSD([subQ6])]})])],"derivedFrom":makeQuery(id+"F1.opExtrude","CAP_FACE",FACE,{"disambiguationData":[OSD([subQ6,subQ8,subQ9,subQ7,subQ4,subQ3,subQ2,subQ1,subQ0,subQ5,subQ10,subQ11])],"isStart":true})});}
            var sketch = newSketch(context, id + "F16", { "sketchPlane" : qUnion([Q0])});
            skLineSegment(sketch, "E79", {"start": v(0, 74.25) * mm, "end": v(0, 104.25) * mm, "construction": true});
            skPoint(sketch, "E79.endSnap0", {"position": v(0, 74.25) * mm});
            skArc(sketch, "E80", {"start": v(15, 104.25) * mm, "mid": v(0, 119.25) * mm, "end": v(-15, 104.25) * mm});
            skLineSegment(sketch, "E81", {"start": v(15, 104.25) * mm, "end": v(15, 92.25) * mm});
            skLineSegment(sketch, "E82", {"start": v(-15, 104.25) * mm, "end": v(-15, 92.25) * mm});
            skLineSegment(sketch, "E83", {"start": v(-15, 92.25) * mm, "end": v(-33, 74.25) * mm});
            skLineSegment(sketch, "E84", {"start": v(15, 92.25) * mm, "end": v(33, 74.25) * mm});
            skCircle(sketch, "E85", {"center": v(0, 104.25) * mm, "radius": 6 * mm});
            skLineSegment(sketch, "E86", {"start": v(-74.25, 0) * mm, "end": v(74.25, 0) * mm, "construction": true});
            skArc(sketch, "E87.MirrorCS", {"start": v(-15, 104.25) * mm, "mid": v(0, 119.25) * mm, "end": v(15, 104.25) * mm});
            skLineSegment(sketch, "E88.MirrorCS", {"start": v(-15, -92.25) * mm, "end": v(-33, -74.25) * mm});
            skLineSegment(sketch, "E89.MirrorCS", {"start": v(-15, -104.25) * mm, "end": v(-15, -92.25) * mm});
            skArc(sketch, "E90.MirrorCS", {"start": v(-15, -104.25) * mm, "mid": v(0, -119.25) * mm, "end": v(15, -104.25) * mm});
            skPoint(sketch, "E91.MirrorP", {"position": v(0, -74.25) * mm});
            skLineSegment(sketch, "E92.MirrorCS", {"start": v(15, -104.25) * mm, "end": v(15, -92.25) * mm});
            skCircle(sketch, "E93.MirrorC", {"center": v(0, -104.25) * mm, "radius": 6 * mm});
            skLineSegment(sketch, "E94.MirrorCS", {"start": v(15, -92.25) * mm, "end": v(33, -74.25) * mm});
            skArc(sketch, "E95.MirrorCS", {"start": v(15, -104.25) * mm, "mid": v(0, -119.25) * mm, "end": v(-15, -104.25) * mm});
            skLineSegment(sketch, "E96.MirrorCS", {"start": v(0, -74.25) * mm, "end": v(0, -104.25) * mm, "construction": true});
            skSolve(sketch);
        }
        {
            var Q0;
            Q0=makeQuery(id+"F16.imprint","IMPRINT",FACE,{"disambiguationData":[TD([[makeQuery(id+"F16.imprint","IMPRINT",EDGE,{"derivedFrom":sQuery(id+"F16.wireOp",EDGE,"E93.MirrorC")}),1.0]])]});
            var Q1;
            Q1=makeQuery(id+"F16.imprint","IMPRINT",FACE,{"disambiguationData":[TD([[makeQuery(id+"F16.imprint","IMPRINT",EDGE,{"derivedFrom":sQuery(id+"F16.wireOp",EDGE,"E82")}),1.0]])]});
            var Q2;
            Q2=makeQuery(id+"F16.imprint","IMPRINT",FACE,{"disambiguationData":[TD([[makeQuery(id+"F16.imprint","IMPRINT",EDGE,{"derivedFrom":makeQuery(id+"F1.opExtrude","CAP_EDGE",EDGE,{"disambiguationData":[OSD([sQuery(id+"F0.wireOp",EDGE,"E1.left")])],"isStart":true})}),-1.0]])]});
            var Q3;
            Q3=makeQuery(id+"F2.opExtrude","CAP_FACE",FACE,{"disambiguationData":[OSD([sQuery(id+"F0.wireOp",EDGE,"E12"),sQuery(id+"F0.wireOp",EDGE,"E13"),sQuery(id+"F0.wireOp",EDGE,"E14"),sQuery(id+"F0.wireOp",EDGE,"E15"),sQuery(id+"F0.wireOp",EDGE,"E17.filletArc"),sQuery(id+"F0.wireOp",EDGE,"E18.filletArc"),sQuery(id+"F0.wireOp",EDGE,"E19.filletArc"),sQuery(id+"F0.wireOp",EDGE,"E20.filletArc"),sQuery(id+"F0.wireOp",EDGE,"E25.0"),sQuery(id+"F0.wireOp",EDGE,"E25.1"),sQuery(id+"F0.wireOp",EDGE,"E25.2"),sQuery(id+"F0.wireOp",EDGE,"E25.3"),sQuery(id+"F0.wireOp",EDGE,"E25.4"),sQuery(id+"F0.wireOp",EDGE,"E25.5"),sQuery(id+"F0.wireOp",EDGE,"E25.6"),sQuery(id+"F0.wireOp",EDGE,"E25.7")])],"isStart":false});
            extrude(context, id + "F17", {"entities" : qUnion([Q0, Q1, Q2]), "endBound" : BoundingType.UP_TO_SURFACE, "endBoundEntityFace" : qUnion([Q3]), "depth" : 25 * mm});
        }
    });
